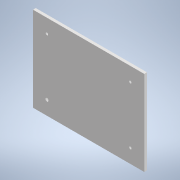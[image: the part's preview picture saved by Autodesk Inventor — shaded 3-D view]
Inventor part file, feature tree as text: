
AUTODESK INVENTOR PART (.ipt)
format: ipt  version: 2020 (Build 240168000, 168)  size: 111,104 bytes
history: native  units: in
note: dims shown in document units (in); Inventor stores cm internally (conversion verified against a paired STEP export)
features: other x3, extrude x1, sketch x1, reference x1
ambient origin geometry x8: Origin, YZ Plane, XZ Plane, XY Plane, X Axis, Y Axis, Z Axis, Center Point
bodies: Body1 (feature_tree)
feature tree (6):
  extrude  "Extrusion2"  Depth=0.1in
  sketch  "Sketch1"  dims[d1=0.5in d2=0.5in d10=0.5in d11=0.5in d12=0.087in d13=0.087in d14=0.087in d15=0.087in d16=0.1in d17=0.0in]
  reference  "Reference1"
  other  "<userpath>\Documents\Inventor\Drone\OdroidAssembly.iam"
  other  "OdroidAssembly.iam"
  other  "odroidstandoff:4"
